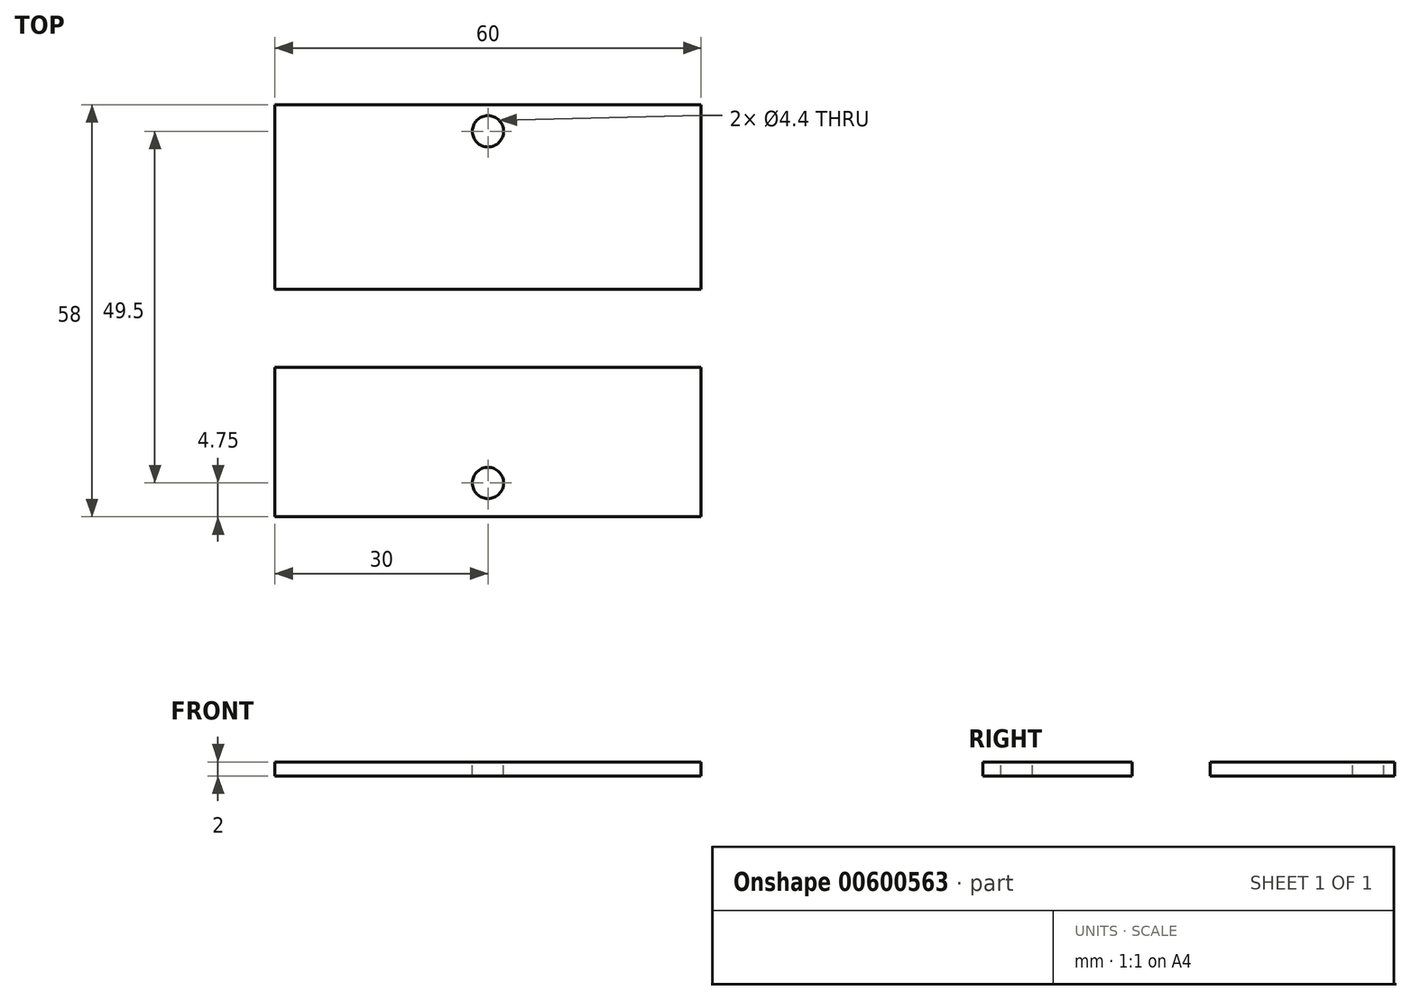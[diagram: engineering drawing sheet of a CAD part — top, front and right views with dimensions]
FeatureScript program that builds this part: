
annotation { "Feature Type Name" : "Feature", "Feature Type Description" : "" }
export const myFeature = defineFeature(function(context is Context, id is Id, definition is map)
    precondition{}
    {
        {
            var Q0;
            Q0=qCreatedBy(makeId("Top.planeOp"),FACE);
            var sketch = newSketch(context, id + "F0", { "sketchPlane" : qUnion([Q0])});
            skLineSegment(sketch, "E0.bottom", {"start": v(-30, 29) * mm, "end": v(30, 29) * mm});
            skLineSegment(sketch, "E0.top", {"start": v(-30, -29) * mm, "end": v(30, -29) * mm});
            skLineSegment(sketch, "E0.left", {"start": v(-30, 29) * mm, "end": v(-30, -29) * mm});
            skLineSegment(sketch, "E0.right", {"start": v(30, 29) * mm, "end": v(30, -29) * mm});
            skPoint(sketch, "E0.middle", {"position": v(0, 0) * mm});
            skLineSegment(sketch, "E1", {"start": v(0, -29) * mm, "end": v(0, -20.5) * mm});
            skPoint(sketch, "E1.endSnap0", {"position": v(0, -29) * mm});
            skLineSegment(sketch, "E2", {"start": v(0, -20.5) * mm, "end": v(0, 29) * mm});
            skLineSegment(sketch, "E3", {"start": v(-17, -29) * mm, "end": v(-17, -8) * mm});
            skLineSegment(sketch, "E4", {"start": v(-17, -8) * mm, "end": v(-30, -8) * mm});
            skLineSegment(sketch, "E5", {"start": v(-30, -8) * mm, "end": v(30, -8) * mm});
            skLineSegment(sketch, "E6", {"start": v(-16.75, 29) * mm, "end": v(-16.75, 3) * mm});
            skLineSegment(sketch, "E7", {"start": v(-16.75, 3) * mm, "end": v(-30, 3) * mm});
            skLineSegment(sketch, "E8", {"start": v(-30, 3) * mm, "end": v(30, 3) * mm});
            skSolve(sketch);
        }
        {
            var Q0;
            {var subQ3=sQuery(id+"F0.wireOp",EDGE,"E6");Q0=makeQuery(id+"F0.imprint","IMPRINT",FACE,{"disambiguationData":[TD([[makeQuery(id+"F0.imprint","IMPRINT",EDGE,{"derivedFrom":subQ3}),-1.0]])]});}
            var Q1;
            {var subQ3=sQuery(id+"F0.wireOp",EDGE,"E6");Q1=makeQuery(id+"F0.imprint","IMPRINT",FACE,{"disambiguationData":[TD([[makeQuery(id+"F0.imprint","IMPRINT",EDGE,{"derivedFrom":subQ3}),1.0]])]});}
            var Q2;
            {var subQ0=sQuery(id+"F0.wireOp",EDGE,"E0.right");var subQ1=sQuery(id+"F0.wireOp",EDGE,"E0.bottom");var subQ2=makeQuery(id+"F0.imprint","INTERSECT",VERTEX,{"derivedFrom":[subQ1,subQ0]});Q2=makeQuery(id+"F0.imprint","IMPRINT",FACE,{"disambiguationData":[TD([[makeQuery(id+"F0.imprint","IMPRINT",EDGE,{"disambiguationData":[TD([[subQ2,1.0]])],"derivedFrom":subQ1}),-1.0]])]});}
            var Q3;
            {var subQ1=sQuery(id+"F0.wireOp",EDGE,"E1");Q3=makeQuery(id+"F0.imprint","IMPRINT",FACE,{"disambiguationData":[TD([[makeQuery(id+"F0.imprint","IMPRINT",EDGE,{"derivedFrom":subQ1}),-1.0]])]});}
            var Q4;
            {var subQ3=sQuery(id+"F0.wireOp",EDGE,"E3");Q4=makeQuery(id+"F0.imprint","IMPRINT",FACE,{"disambiguationData":[TD([[makeQuery(id+"F0.imprint","IMPRINT",EDGE,{"derivedFrom":subQ3}),1.0]])]});}
            var Q5;
            {var subQ2=sQuery(id+"F0.wireOp",EDGE,"E1");Q5=makeQuery(id+"F0.imprint","IMPRINT",FACE,{"disambiguationData":[TD([[makeQuery(id+"F0.imprint","IMPRINT",EDGE,{"derivedFrom":subQ2}),1.0]])]});}
            extrude(context, id + "F1", {"entities" : qUnion([Q0, Q1, Q2, Q3, Q4, Q5]), "depth" : 2 * mm, "offsetDistance" : 25 * mm});
        }
        {
            var Q0;
            Q0=makeQuery(id+"F1.opExtrude","CAP_FACE",FACE,{"disambiguationData":[OSD([sQuery(id+"F0.wireOp",EDGE,"E0.top"),sQuery(id+"F0.wireOp",EDGE,"E0.left"),sQuery(id+"F0.wireOp",EDGE,"E0.right"),sQuery(id+"F0.wireOp",EDGE,"E5")])],"isStart":false});
            var sketch = newSketch(context, id + "F2", { "sketchPlane" : qUnion([Q0])});
            skLineSegment(sketch, "E9", {"start": v(0, -29) * mm, "end": v(0, -24.25) * mm});
            skPoint(sketch, "E9.endSnap0", {"position": v(0, -29) * mm});
            skLineSegment(sketch, "E10", {"start": v(0, -24.25) * mm, "end": v(0, 25.25) * mm});
            skSolve(sketch);
        }
        {
            var Q0;
            Q0=sQuery(id+"F2.wireOp",VERTEX,"E10.end");
            var Q1;
            Q1=sQuery(id+"F2.wireOp",VERTEX,"E10.start");
            var Q2;
            Q2=makeQuery(id+"F1.opExtrude","SWEPT_BODY",BODY,{"disambiguationData":[OSD([sQuery(id+"F0.wireOp",EDGE,"E0.bottom"),sQuery(id+"F0.wireOp",EDGE,"E0.left"),sQuery(id+"F0.wireOp",EDGE,"E0.right"),sQuery(id+"F0.wireOp",EDGE,"E8")])]});
            var Q3;
            Q3=makeQuery(id+"F1.opExtrude","SWEPT_BODY",BODY,{"disambiguationData":[OSD([sQuery(id+"F0.wireOp",EDGE,"E0.top"),sQuery(id+"F0.wireOp",EDGE,"E0.left"),sQuery(id+"F0.wireOp",EDGE,"E0.right"),sQuery(id+"F0.wireOp",EDGE,"E5")])]});
            hole(context, id + "F3", {"style" : HoleStyle.C_BORE, "endStyle" : HoleEndStyle.THROUGH, "holeDiameter" : 4.4 * mm, "cBoreDiameter" : 8.25 * mm, "cBoreDepth" : 0 * mm, "majorDiameter" : 5 * mm, "isTappedThrough" : true, "tappedDepth" : 12 * mm, "tapClearance" : 3, "locations" : qUnion([Q0, Q1]), "scope" : qUnion([Q2, Q3])});
        }
    });
